# Revit family: Valve-Control-Waterworks-Universal-Counter_Clockwise
name_source: partatom
category: Pipe Accessories
revit_build: Autodesk Revit MEP 2014 (Build: 20140709_2115(x64)
units: mm (PartAtom-declared; Revit-internal decimal feet)

## types (1)
- 1/2” Counter-Clockwise Volume Control Valve
    ADA Compliant = Yes
    Anti-scald Protection = No
    Assembly Code = D2010
    Certification IAPMO = Yes
    Certification State of MA = Yes
    Certification cUPC = Yes
    Code Compliance = Code # GUSV18:
    Depth = 0' - 6 15/16"
    Description = Universal 1/2” Counter-Clockwise On Volume Control Valve
    Finish = Metal - Waterworks - Unfinished
    Fittings Hole Diameter = 0' - 1 3/8"
    Height = 0' - 2 9/16"
    Keynote = 22 40 00
    Length = 0' - 1"
    Manufacturer = Waterworks
    Mixed Water Inlet Diameter = 0' - 0 1/2"
    Mixed Water Outlet Bottom Connection = Inlet - Female NPT
    Mixed Water Outlet Diameter = 0' - 0 1/2"
    Mixed Water ‌Outlet Connection = Outlet - Female NPT
    Model = GUVC18
    Model SKU = 26-03622-54601
    Pressure = 45.00 psi
    Product Documentation Link = http://assets.waterworks.com
    Product Name = Universal 1/2” Counter-Clockwise On Volume Control Valve
    Product Page URL = http://www.waterworks.com
    URL = http://www.waterworks.com
    Version = 2014 - v1.0a
    Warranty = http://www.waterworks.com
    Water Pressure = Max: 85psi / Min: 20psi / Recommended: 45psi
    ‌Installation Requirements or Notes = Valve rough-in depth is measured from the center of the inlets to the surface of the finished wall and varies depending on the trim used

## geometry (parser evidence)
native form markers: Sweep x1
no freeform markers — native parametric forms only
